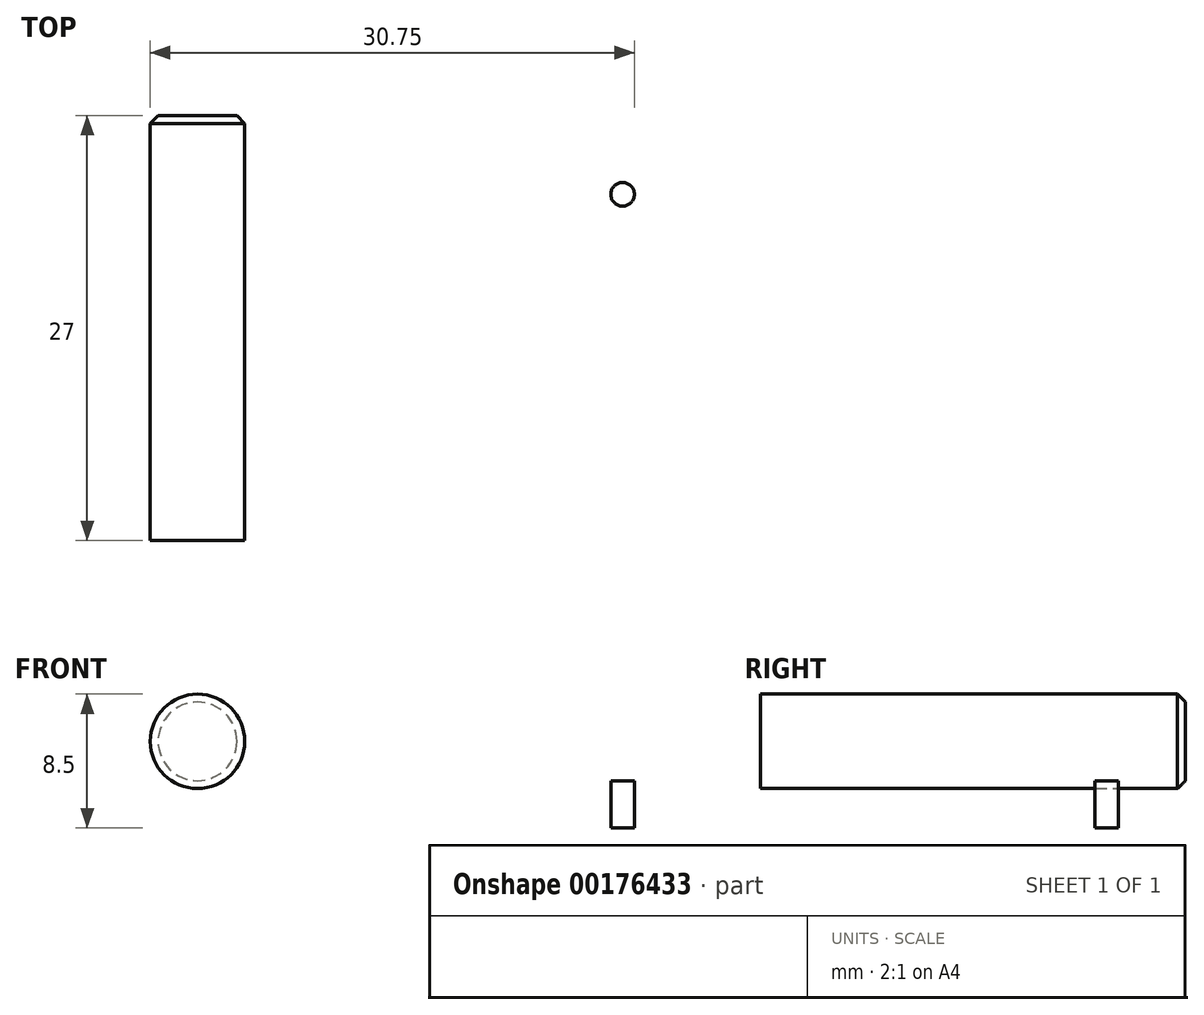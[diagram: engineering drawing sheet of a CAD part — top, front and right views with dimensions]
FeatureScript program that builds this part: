
annotation { "Feature Type Name" : "Feature", "Feature Type Description" : "" }
export const myFeature = defineFeature(function(context is Context, id is Id, definition is map)
    precondition{}
    {
        {
            var Q0;
            Q0=qCreatedBy(makeId("Front.planeOp"),FACE);
            var sketch = newSketch(context, id + "F0", { "sketchPlane" : qUnion([Q0])});
            skLineSegment(sketch, "E0", {"start": v(0, 0) * mm, "end": v(0, 7.5) * mm});
            skCircle(sketch, "E1", {"center": v(-13.5, 7.5) * mm, "radius": 3 * mm});
            skCircle(sketch, "E2.MirrorC", {"center": v(13.5, 7.5) * mm, "radius": 3 * mm});
            skSolve(sketch);
        }
        {
            var Q0;
            Q0=makeQuery(id+"F0.imprint","IMPRINT",FACE,{"disambiguationData":[TD([[makeQuery(id+"F0.imprint","IMPRINT",EDGE,{"derivedFrom":sQuery(id+"F0.wireOp",EDGE,"E1")}),1.0]])]});
            var Q1;
            Q1=makeQuery(id+"F0.imprint","IMPRINT",FACE,{"disambiguationData":[TD([[makeQuery(id+"F0.imprint","IMPRINT",EDGE,{"derivedFrom":sQuery(id+"F0.wireOp",EDGE,"E2.MirrorC")}),-1.0]])]});
            extrude(context, id + "F1", {"entities" : qUnion([Q0, Q1]), "depth" : 27 * mm});
        }
        {
            var Q0;
            Q0=makeQuery(id+"F1.opExtrude","CAP_EDGE",EDGE,{"disambiguationData":[OSD([sQuery(id+"F0.wireOp",EDGE,"E1")])],"isStart":true});
            var Q1;
            Q1=makeQuery(id+"F1.opExtrude","CAP_EDGE",EDGE,{"disambiguationData":[OSD([sQuery(id+"F0.wireOp",EDGE,"E2.MirrorC")])],"isStart":true});
            chamfer(context, id + "F2", {"entities" : qUnion([Q0, Q1]), "width" : .5 * mm, "tangentPropagation" : true});
        }
        {
            var Q0;
            Q0=qCreatedBy(makeId("Top.planeOp"),FACE);
            var sketch = newSketch(context, id + "F3", { "sketchPlane" : qUnion([Q0])});
            skLineSegment(sketch, "E3", {"start": v(0, 0) * mm, "end": v(0, -5) * mm});
            skLineSegment(sketch, "E4", {"start": v(0, -5) * mm, "end": v(13.5, -5) * mm});
            skCircle(sketch, "E5", {"center": v(13.5, -5) * mm, "radius": 0.75 * mm});
            skSolve(sketch);
        }
        {
            var Q0;
            Q0 = qSketchRegion(id + "F3", true);
            extrude(context, id + "F4", {"entities" : qUnion([Q0]), "operationType" : NewBodyOperationType.ADD, "depth" : 5 * mm, "hasSecondDirection" : true, "secondDirectionOppositeDirection" : false, "secondDirectionDepth" : 2 * mm});
        }
    });
